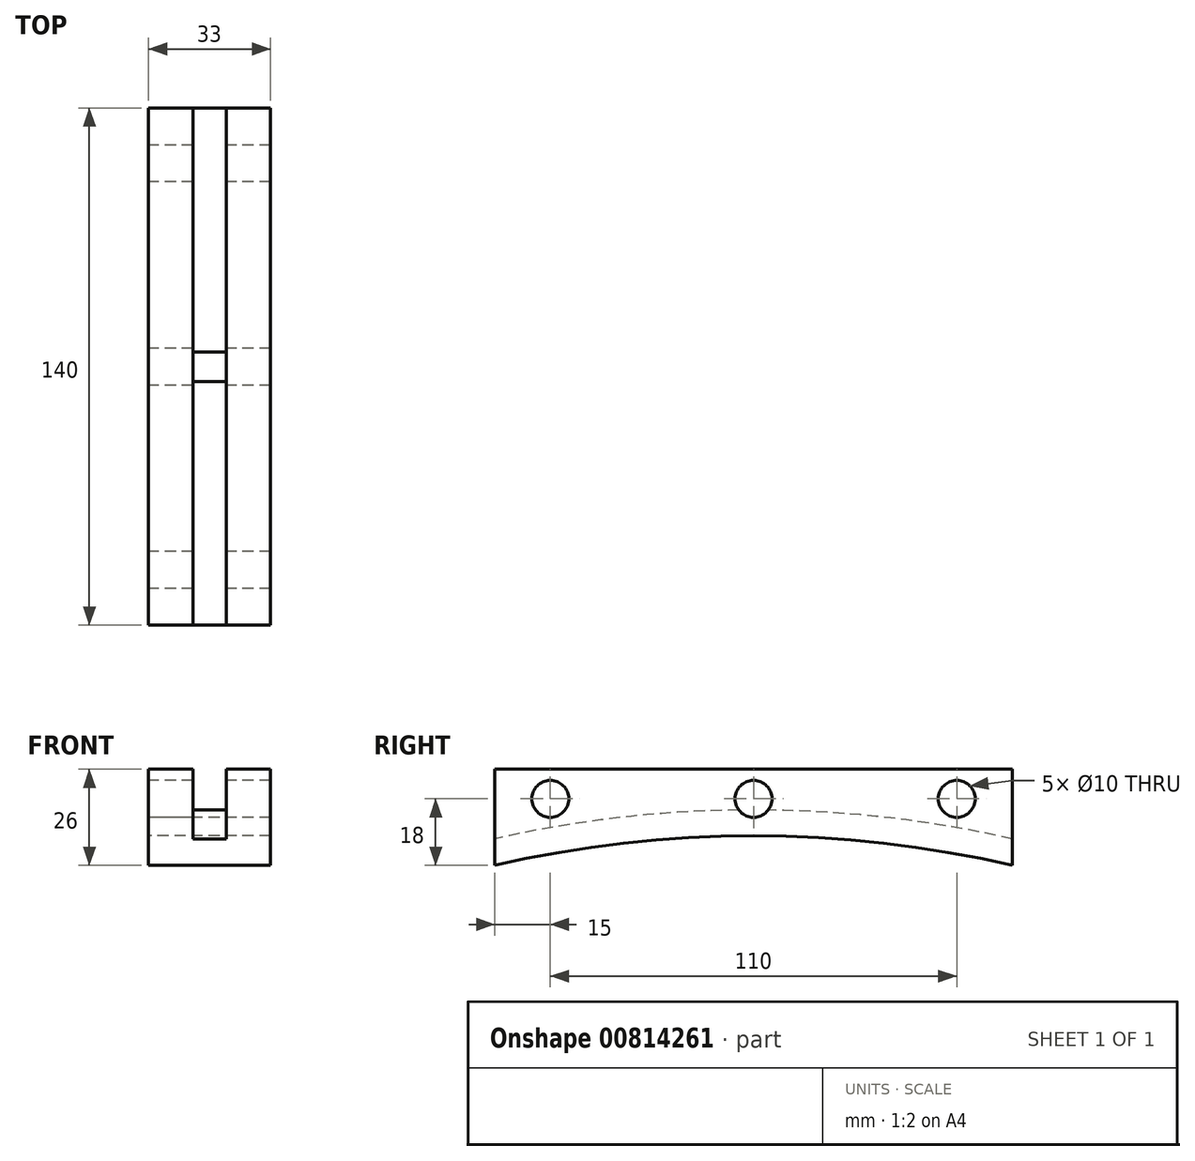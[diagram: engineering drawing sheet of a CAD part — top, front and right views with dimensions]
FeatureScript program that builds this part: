
annotation { "Feature Type Name" : "Feature", "Feature Type Description" : "" }
export const myFeature = defineFeature(function(context is Context, id is Id, definition is map)
    precondition{}
    {
        {
            var Q0;
            Q0=qCreatedBy(makeId("Right.planeOp"),FACE);
            var sketch = newSketch(context, id + "F0", { "sketchPlane" : qUnion([Q0])});
            skLineSegment(sketch, "E0.bottom", {"start": v(-70, 0) * mm, "end": v(70, 0) * mm});
            skLineSegment(sketch, "E0.top", {"start": v(-70, 26) * mm, "end": v(70, 26) * mm});
            skLineSegment(sketch, "E0.left", {"start": v(-70, 0) * mm, "end": v(-70, 26) * mm});
            skLineSegment(sketch, "E0.right", {"start": v(70, 0) * mm, "end": v(70, 26) * mm});
            skLineSegment(sketch, "E1", {"start": v(0, 26) * mm, "end": v(0, 8) * mm});
            skArc(sketch, "E2", {"start": v(70, 0) * mm, "mid": v(0, 8) * mm, "end": v(-70, 0) * mm});
            skCircle(sketch, "E3", {"center": v(-55, 18) * mm, "radius": 5 * mm});
            skCircle(sketch, "E4", {"center": v(55, 18) * mm, "radius": 5 * mm});
            skCircle(sketch, "E5", {"center": v(0, 18) * mm, "radius": 5 * mm});
            skArc(sketch, "E6.0", {"start": v(71.58, 6.82) * mm, "mid": v(0, 15) * mm, "end": v(-71.58, 6.82) * mm});
            skSolve(sketch);
        }
        {
            var Q0;
            {var subQ5=sQuery(id+"F0.wireOp",EDGE,"E0.right");Q0=makeQuery(id+"F0.imprint","IMPRINT",FACE,{"disambiguationData":[TD([[makeQuery(id+"F0.imprint","IMPRINT",EDGE,{"derivedFrom":subQ5}),1.0]])]});}
            var Q1;
            Q1=makeQuery(id+"F0.imprint","IMPRINT",FACE,{"disambiguationData":[TD([[makeQuery(id+"F0.imprint","IMPRINT",EDGE,{"derivedFrom":sQuery(id+"F0.wireOp",EDGE,"E3")}),-1.0]])]});
            var Q2;
            Q2=makeQuery(id+"F0.imprint","IMPRINT",FACE,{"disambiguationData":[TD([[makeQuery(id+"F0.imprint","IMPRINT",EDGE,{"derivedFrom":sQuery(id+"F0.wireOp",EDGE,"E4")}),-1.0]])]});
            var Q3;
            {var subQ1=sQuery(id+"F0.wireOp",EDGE,"E1");var subQ5=sQuery(id+"F0.wireOp",EDGE,"E2");var subQ8=makeQuery(id+"F0.imprint","INTERSECT",VERTEX,{"derivedFrom":[subQ1,subQ5]});Q3=makeQuery(id+"F0.imprint","IMPRINT",FACE,{"disambiguationData":[TD([[makeQuery(id+"F0.imprint","IMPRINT",EDGE,{"disambiguationData":[TD([[subQ8,1.0]])],"derivedFrom":subQ1}),-1.0]])]});}
            extrude(context, id + "F1", {"entities" : qUnion([Q0, Q1, Q2, Q3]), "depth" : 33 * mm, "offsetDistance" : 25 * mm});
        }
        {
            var Q0;
            Q0=makeQuery(id+"F1.opExtrude","SWEPT_FACE",FACE,{"disambiguationData":[OSD([sQuery(id+"F0.wireOp",EDGE,"E0.left")])]});
            var sketch = newSketch(context, id + "F2", { "sketchPlane" : qUnion([Q0])});
            skLineSegment(sketch, "E7", {"start": v(0, 26) * mm, "end": v(12, 26) * mm});
            skLineSegment(sketch, "E8", {"start": v(12, 26) * mm, "end": v(12, 7) * mm});
            skLineSegment(sketch, "E9", {"start": v(12, 7) * mm, "end": v(21, 7) * mm});
            skLineSegment(sketch, "E10", {"start": v(21, 7) * mm, "end": v(21, 26) * mm});
            skLineSegment(sketch, "E11", {"start": v(21, 26) * mm, "end": v(33, 26) * mm});
            skSolve(sketch);
        }
        {
            var Q0;
            Q0 = qSketchRegion(id + "F2", true);
            var Q1;
            {var subQ0=sQuery(id+"F2.wireOp",EDGE,"E8");Q1=makeQuery(id+"F2.imprint","IMPRINT",FACE,{"disambiguationData":[TD([[makeQuery(id+"F2.imprint","IMPRINT",EDGE,{"derivedFrom":subQ0}),1.0]])]});}
            extrude(context, id + "F3", {"entities" : qUnion([Q0, Q1]), "operationType" : NewBodyOperationType.REMOVE, "oppositeDirection" : true, "depth" : 140 * mm, "offsetDistance" : 25 * mm});
        }
        {
            var Q0;
            Q0=makeQuery(id+"F1.opExtrude","CAP_FACE",FACE,{"disambiguationData":[OSD([sQuery(id+"F0.wireOp",EDGE,"E0.top"),sQuery(id+"F0.wireOp",EDGE,"E0.left"),sQuery(id+"F0.wireOp",EDGE,"E0.right"),sQuery(id+"F0.wireOp",EDGE,"E2"),sQuery(id+"F0.wireOp",EDGE,"E3"),sQuery(id+"F0.wireOp",EDGE,"E4"),sQuery(id+"F0.wireOp",EDGE,"E5")])],"isStart":false});
            var sketch = newSketch(context, id + "F4", { "sketchPlane" : qUnion([Q0])});
            skArc(sketch, "E12.0", {"start": v(70.8, 7) * mm, "mid": v(0, 15) * mm, "end": v(-70.8, 7) * mm});
            skSolve(sketch);
        }
        {
            var Q0;
            Q0 = qSketchRegion(id + "F4", true);
            var Q1;
            {var subQ0=makeQuery(id+"F1.opExtrude","CAP_EDGE",EDGE,{"disambiguationData":[OSD([sQuery(id+"F0.wireOp",EDGE,"E2")])],"isStart":false});Q1=makeQuery(id+"F4.imprint","IMPRINT",FACE,{"disambiguationData":[TD([[makeQuery(id+"F4.imprint","IMPRINT",EDGE,{"derivedFrom":subQ0}),-1.0]])]});}
            extrude(context, id + "F5", {"entities" : qUnion([Q0, Q1]), "operationType" : NewBodyOperationType.ADD, "oppositeDirection" : true, "depth" : 33 * mm, "offsetDistance" : 25 * mm});
        }
    });
